# Revit family: 145-50-001 DN65-200
name_source: partatom
category: Pipe Accessories
units: mm (PartAtom-declared; Revit-internal decimal feet)

## family parameters
Always vertical = No
Cut with Voids When Loaded = No
Part Type = Valve - Breaks Into
Round Connector Dimension = Use Diameter
Shared = No
Work Plane-Based = No

## types (6) — shared parameters
0 = 0.01 mm  [stored 3.2808e-05 ft]
1 = 1 mm  [stored 0.00328084 ft]
5 = 5 mm  [stored 0.0164042 ft]
DN065_PN10/16 = 145-065-50-01396100
DN080_PN10/16 = 145-080-50-01396100
DN100_PN10/16 = 145-100-50-01396100
DN150_PN10/16 = 145-150-50-01396100
DN200_PN10 = 145-200-50-00396100
DN200_PN16 = 145-200-50-01396100
Description_ = AVK GATE VALVE, FLANGED, NRS, 250 PSI/17.2 BAR
Search_table = 145-50-001 DN65-200
URL product pages = https://www.avkvalves.com
zero-valued in all types: Default Elevation

## per-type parameters (varying)
- DN200_PN16: Body_FL_L=176 mm; Body_FL_W=95 mm; Body_H=220 mm; Body_L=166 mm; Body_T=11 mm  [stored 0.0360892 ft]; Body_W=85 mm; Body_rib_L=75 mm; Body_wedge_dim=40.02 mm; Bonnet1=190 mm; Bonnet2=51 mm; Bonnet3=35.7 mm; Bonnet4=83 mm; Bonnet5=59.5 mm; Bonnet_H=160 mm; Bonnet_dim=212.1 mm; Bonnet_dim1=198.9 mm; Bonnet_dim2=53.55 mm; Bore_R=100.05 mm; DN=200.1 mm; FL_OD=176 mm; FL_T=29 mm; H=502 mm; H3=674 mm; L=292 mm; Logo_H.=22 mm; Raised_R1=137.28 mm; Rib1_H=70 mm; Rib1_L=176 mm; Rib1_R=35 mm; Rib1_W=95 mm; Rib2_H=110 mm; Rib2_L=176 mm; Rib2_W=95 mm; Rib_T=6 mm  [stored 0.019685 ft]; Stem_cap1=34 mm; Stem_cap2=29.75 mm; Stem_cap_H1=55 mm; Stem_cap_H2=45.5 mm; Stem_cap_H3=65 mm; Stem_cap_dim1=47.22 mm; W=176 mm; stem_R=20.83 mm
- DN200_PN10: Body_FL_L=176 mm; Body_FL_W=95 mm; Body_H=220 mm; Body_L=166 mm; Body_T=11 mm  [stored 0.0360892 ft]; Body_W=85 mm; Body_rib_L=75 mm; Body_wedge_dim=40 mm; Bonnet1=190 mm; Bonnet2=51 mm; Bonnet3=35.7 mm; Bonnet4=83 mm; Bonnet5=59.5 mm; Bonnet_H=160 mm; Bonnet_dim=212.1 mm; Bonnet_dim1=198.9 mm; Bonnet_dim2=53.55 mm; Bore_R=100 mm; DN=200 mm; FL_OD=176 mm; FL_T=29 mm; H=502 mm; H3=674 mm; L=292 mm; Logo_H.=22 mm; Raised_R1=137.28 mm; Rib1_H=70 mm; Rib1_L=176 mm; Rib1_R=35 mm; Rib1_W=95 mm; Rib2_H=110 mm; Rib2_L=176 mm; Rib2_W=95 mm; Rib_T=6 mm  [stored 0.019685 ft]; Stem_cap1=34 mm; Stem_cap2=29.75 mm; Stem_cap_H1=55 mm; Stem_cap_H2=45.5 mm; Stem_cap_H3=65 mm; Stem_cap_dim1=47.22 mm; W=176 mm; stem_R=20.83 mm
- DN150_PN10/16: Body_FL_L=135 mm; Body_FL_W=77 mm; Body_H=173 mm; Body_L=127 mm; Body_T=9 mm  [stored 0.0295276 ft]; Body_W=51.5 mm; Body_rib_L=65 mm; Body_wedge_dim=30 mm; Bonnet1=150 mm; Bonnet2=30.9 mm; Bonnet3=21.63 mm; Bonnet4=63.5 mm; Bonnet5=36.05 mm; Bonnet_H=125 mm; Bonnet_dim=171.7 mm; Bonnet_dim1=159.3 mm; Bonnet_dim2=32.45 mm; Bore_R=75 mm; DN=150 mm; FL_OD=140 mm; FL_T=25 mm; H=409 mm; H3=549 mm; L=267 mm; Logo_H.=17.3 mm  [stored 0.0567585 ft]; Raised_R1=109.2 mm; Rib1_H=50 mm; Rib1_L=135 mm; Rib1_R=30 mm; Rib1_W=77.5 mm; Rib2_H=30 mm; Rib2_L=60 mm; Rib2_W=50 mm; Rib_T=4.5 mm  [stored 0.0147638 ft]; Stem_cap1=20.6 mm; Stem_cap2=18.03 mm; Stem_cap_H1=50 mm; Stem_cap_H2=42 mm; Stem_cap_H3=60 mm; Stem_cap_dim1=28.61 mm; W=140 mm; stem_R=12.62 mm
- DN100_PN10/16: Body_FL_L=96 mm; Body_FL_W=52.5 mm; Body_H=122 mm; Body_L=82 mm; Body_T=6 mm  [stored 0.019685 ft]; Body_W=38 mm; Body_rib_L=50 mm; Body_wedge_dim=20 mm  [stored 0.0656168 ft]; Bonnet1=105 mm; Bonnet2=22.8 mm  [stored 0.0748031 ft]; Bonnet3=15.96 mm  [stored 0.0523622 ft]; Bonnet4=41 mm; Bonnet5=26.6 mm; Bonnet_H=82 mm; Bonnet_dim=141.4 mm; Bonnet_dim1=114.3 mm; Bonnet_dim2=23.94 mm  [stored 0.0785433 ft]; Bore_R=50 mm; DN=100 mm; FL_OD=114.5 mm; FL_T=24 mm  [stored 0.0787402 ft]; H=322 mm; H3=436 mm; L=229 mm; Logo_H.=12.2 mm  [stored 0.0400262 ft]; Raised_R1=89.31 mm; Rib1_H=25 mm; Rib1_L=35 mm; Rib1_R=25 mm; Rib1_W=30 mm; Rib2_H=30 mm; Rib2_L=30 mm; Rib2_W=30 mm; Rib_T=5 mm  [stored 0.0164042 ft]; Stem_cap1=15.2 mm; Stem_cap2=13.3 mm  [stored 0.0436352 ft]; Stem_cap_H1=45 mm; Stem_cap_H2=38.5 mm; Stem_cap_H3=55 mm; Stem_cap_dim1=21.11 mm; W=114.5 mm; stem_R=9.31 mm  [stored 0.0305446 ft]
- DN080_PN10/16: Body_FL_L=85.5 mm; Body_FL_W=48 mm; Body_H=108 mm; Body_L=72 mm; Body_T=6 mm  [stored 0.019685 ft]; Body_W=35 mm; Body_rib_L=45 mm; Body_wedge_dim=16 mm  [stored 0.0524934 ft]; Bonnet1=86.25 mm; Bonnet2=21 mm  [stored 0.0688976 ft]; Bonnet3=14.7 mm  [stored 0.0482283 ft]; Bonnet4=36 mm; Bonnet5=24.5 mm  [stored 0.0803806 ft]; Bonnet_H=72 mm; Bonnet_dim=116.15 mm; Bonnet_dim1=105.3 mm; Bonnet_dim2=22.05 mm  [stored 0.0723425 ft]; Bore_R=40 mm; DN=80 mm; FL_OD=95.5 mm; FL_T=20 mm  [stored 0.0656168 ft]; H=304 mm; H3=399 mm; L=203 mm; Logo_H.=10.8 mm  [stored 0.0354331 ft]; Raised_R1=74.49 mm; Rib1_H=25 mm; Rib1_L=30 mm; Rib1_R=20 mm  [stored 0.0656168 ft]; Rib1_W=30 mm; Rib2_H=30 mm; Rib2_L=30 mm; Rib2_W=30 mm; Rib_T=5 mm  [stored 0.0164042 ft]; Stem_cap1=14 mm  [stored 0.0459318 ft]; Stem_cap2=12.25 mm  [stored 0.0401903 ft]; Stem_cap_H1=45 mm; Stem_cap_H2=38.5 mm; Stem_cap_H3=55 mm; Stem_cap_dim1=19.44 mm; W=95.5 mm; stem_R=8.58 mm
- DN065_PN10/16: Body_FL_L=76 mm; Body_FL_W=46 mm; Body_H=95 mm; Body_L=60 mm; Body_T=6 mm  [stored 0.019685 ft]; Body_W=35 mm; Body_rib_L=45 mm; Body_wedge_dim=13 mm; Bonnet1=75 mm; Bonnet2=21 mm  [stored 0.0688976 ft]; Bonnet3=14.7 mm  [stored 0.0482283 ft]; Bonnet4=30 mm; Bonnet5=24.5 mm  [stored 0.0803806 ft]; Bonnet_H=60 mm; Bonnet_dim=101 mm; Bonnet_dim1=90 mm; Bonnet_dim2=22.05 mm  [stored 0.0723425 ft]; Bore_R=32.5 mm; DN=65 mm; FL_OD=89 mm; FL_T=10 mm  [stored 0.0328084 ft]; H=267 mm; H3=356 mm; L=190 mm; Logo_H.=9.5 mm  [stored 0.031168 ft]; Raised_R1=69.42 mm; Rib1_H=25 mm; Rib1_L=30 mm; Rib1_R=15 mm  [stored 0.0492126 ft]; Rib1_W=30 mm; Rib2_H=30 mm; Rib2_L=30 mm; Rib2_W=17.5 mm  [stored 0.0574147 ft]; Rib_T=5 mm  [stored 0.0164042 ft]; Stem_cap1=14 mm  [stored 0.0459318 ft]; Stem_cap2=12.25 mm  [stored 0.0401903 ft]; Stem_cap_H1=40 mm; Stem_cap_H2=35 mm; Stem_cap_H3=50 mm; Stem_cap_dim1=19.44 mm; W=89 mm; stem_R=8.58 mm

note: [stored X ft] marks values corroborated as IEEE doubles in the binary element streams (Revit-internal decimal feet)

## geometry (parser evidence)
native form markers: Sweep x6
no freeform markers — native parametric forms only
